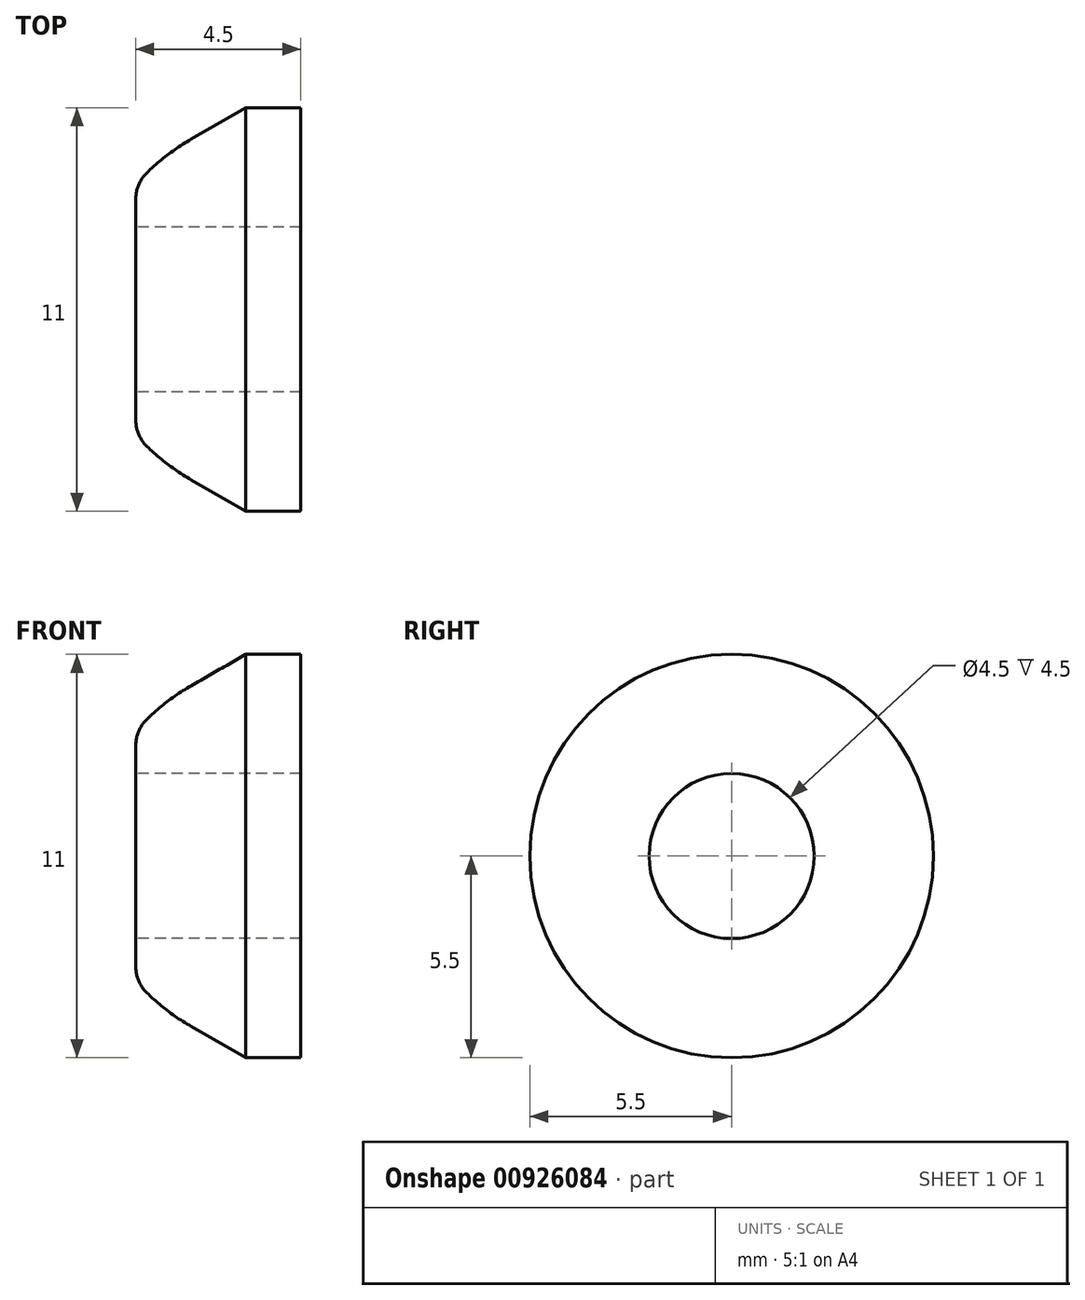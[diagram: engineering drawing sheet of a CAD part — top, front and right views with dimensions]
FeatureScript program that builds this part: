
annotation { "Feature Type Name" : "Feature", "Feature Type Description" : "" }
export const myFeature = defineFeature(function(context is Context, id is Id, definition is map)
    precondition{}
    {
        {
            var Q0;
            Q0=qCreatedBy(makeId("Front.planeOp"),FACE);
            var sketch = newSketch(context, id + "F0", { "sketchPlane" : qUnion([Q0])});
            skLineSegment(sketch, "E0", {"start": v(0, 0) * mm, "end": v(0, 2.36) * mm});
            skLineSegment(sketch, "E1", {"start": v(-0.22, 2.65) * mm, "end": v(-1.8, 3.07) * mm});
            skLineSegment(sketch, "E2", {"start": v(-2.2, 3.13) * mm, "end": v(-2.73, 3.13) * mm});
            skPoint(sketch, "E3.visualSharp", {"position": v(-2, 3.13) * mm});
            skArc(sketch, "E3.filletArc", {"start": v(-1.8, 3.07) * mm, "mid": v(-2, 3.11) * mm, "end": v(-2.2, 3.12) * mm});
            skPoint(sketch, "E4.visualSharp", {"position": v(0, 2.59) * mm});
            skArc(sketch, "E4.filletArc", {"start": v(0, 2.36) * mm, "mid": v(-0.06, 2.54) * mm, "end": v(-0.22, 2.65) * mm});
            skLineSegment(sketch, "E5", {"start": v(0, 0) * mm, "end": v(0, 2.25) * mm});
            skPoint(sketch, "E6.newPointA", {"position": v(-4, 0) * mm});
            skArc(sketch, "E6.filletArc", {"start": v(-4.53, 3.95) * mm, "mid": v(-4.29, 3.37) * mm, "end": v(-3.7, 3.12) * mm});
            skLineSegment(sketch, "E7", {"start": v(-4.53, 3.95) * mm, "end": v(-4.53, 0) * mm});
            skLineSegment(sketch, "E8", {"start": v(-3.17, 3.13) * mm, "end": v(-3.02, 2.88) * mm});
            skLineSegment(sketch, "E9.trimOffspring", {"start": v(-3.17, 3.13) * mm, "end": v(-3.7, 3.13) * mm});
            skLineSegment(sketch, "E10.MirrorCS", {"start": v(-2.88, 3.13) * mm, "end": v(-3.02, 2.88) * mm});
            skLineSegment(sketch, "E11", {"start": v(0, 2.25) * mm, "end": v(-2.25, 0) * mm});
            skLineSegment(sketch, "E12", {"start": v(-9.27, 11) * mm, "end": v(-10.76, 10.14) * mm});
            skLineSegment(sketch, "E13", {"start": v(-9.27, 11) * mm, "end": v(-7.77, 11) * mm});
            skLineSegment(sketch, "E14", {"start": v(-7.77, 11) * mm, "end": v(-7.77, 7.75) * mm});
            skLineSegment(sketch, "E15", {"start": v(-12.27, 5.5) * mm, "end": v(-7.77, 5.5) * mm});
            skLineSegment(sketch, "E16", {"start": v(-12.27, 8.51) * mm, "end": v(-12.27, 7.75) * mm});
            skPoint(sketch, "E17.orphan", {"position": v(-7.77, 0.5) * mm});
            skLineSegment(sketch, "E18.trimOffspring", {"start": v(-9.27, 7.75) * mm, "end": v(-9.27, 11) * mm});
            skPoint(sketch, "E19.end.orphan", {"position": v(-9.27, 0.5) * mm});
            skPoint(sketch, "E19.start.orphan", {"position": v(-9.27, 0) * mm});
            skLineSegment(sketch, "E20", {"start": v(-12.27, 5.5) * mm, "end": v(7.08, 5.5) * mm, "construction": true});
            skLineSegment(sketch, "E21", {"start": v(-12.27, 7.75) * mm, "end": v(-7.77, 7.75) * mm});
            skArc(sketch, "E22", {"start": v(-41.3, 17.21) * mm, "mid": v(-40.74, 17.44) * mm, "end": v(-41.33, 17.35) * mm});
            skArc(sketch, "E23", {"start": v(-41.37, 17.35) * mm, "mid": v(-41.33, 17.28) * mm, "end": v(-41.3, 17.21) * mm});
            skLineSegment(sketch, "E24", {"start": v(-17.92, 17.9) * mm, "end": v(-41.03, 17.36) * mm});
            skLineSegment(sketch, "E25", {"start": v(-26.54, 17.7) * mm, "end": v(-41.03, 17.36) * mm});
            skArc(sketch, "E26", {"start": v(-2.05, 3.12) * mm, "mid": v(-1.8, 4.3) * mm, "end": v(-1.8, 5.5) * mm});
            skPoint(sketch, "E27.orphan", {"position": v(-12.27, 9.28) * mm});
            skPoint(sketch, "E28.visualSharp", {"position": v(-12.27, 8.91) * mm});
            skArc(sketch, "E28.filletArc", {"start": v(-11.97, 9.23) * mm, "mid": v(-12.2, 8.9) * mm, "end": v(-12.27, 8.51) * mm});
            skArc(sketch, "E29.trimOffspring", {"start": v(-10.76, 10.14) * mm, "mid": v(-11.4, 9.72) * mm, "end": v(-11.97, 9.23) * mm});
            skSolve(sketch);
        }
        {
            var Q0;
            Q0 = qSketchRegion(id + "F0", true);
            var Q1;
            Q1=sQuery(id+"F0.wireOp",EDGE,"E15");
            revolve(context, id + "F1", {"surfaceOperationType" : NewSurfaceOperationType.NEW, "entities" : qUnion([Q0]), "axis" : qUnion([Q1]), "revolveType" : RevolveType.FULL});
        }
    });
